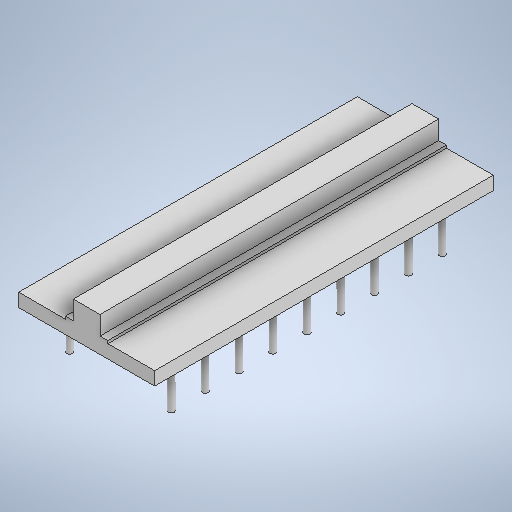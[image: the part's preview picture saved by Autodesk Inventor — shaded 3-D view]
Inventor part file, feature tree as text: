
AUTODESK INVENTOR PART (.ipt)
format: ipt  version: 2025 (Build 290162000, 162)  size: 386,048 bytes
history: native  units: in
note: dims shown in document units (in); Inventor stores cm internally (conversion verified against a paired STEP export)
features: extrude x5, sketch x5
ambient origin geometry x8: Origin, YZ Plane, XZ Plane, XY Plane, X Axis, Y Axis, Z Axis, Center Point
bodies: Solid1 (feature_tree)
feature tree (10):
  extrude  "Extrusion1"  Depth=1.0in
  extrude  "Extrusion3"  Depth=0.0394in
  extrude  "Extrusion4"  Depth=0.15in
  extrude  "Extrusion5"  Depth=0.0394in
  extrude  "Extrusion6"  Depth=0.0551in
  sketch  "Sketch1"  dims[d0=0.4016in d1=1.0in]
  sketch  "Sketch2"  dims[d2=0.0394in d3=0.0in d4=0.2008in]
  sketch  "Sketch3"  dims[d5=90.0deg d6=0.15in]
  sketch  "Sketch5"  dims[d7=0.1in d8=0.0394in]
  sketch  "Sketch6"  dims[d9=0.1in d10=0.1in d11=0.1in d12=0.1in d13=0.1in d14=0.1in d15=0.1in d16=0.1in d17=0.0394in d18=0.0394in d19=0.0394in d20=0.0394in d21=0.0394in d22=0.0394in d23=0.0394in d24=0.0394in d27=0.0177in d28=0.0177in d29=0.0177in d30=0.0177in d31=0.0177in d32=0.0177in d33=0.0177in d34=0.0177in d35=0.0177in d36=0.1378in d37=0.0in d38=0.0394in d39=0.0394in d40=0.0394in d41=0.0394in d42=0.0394in d43=0.0394in d44=0.0394in d45=0.0394in d46=0.0394in d47=0.0394in d48=0.0394in d49=0.0394in d50=0.0394in d51=0.0394in d52=0.0394in d53=0.0394in d54=0.0394in d55=0.0394in d56=0.0039in d57=0.0in d61=0.5in d62=0.2008in d63=0.1252in d64=0.0079in d65=0.0in d66=0.5in d67=0.2008in d68=0.0787in d69=0.0551in d70=0.0in]
